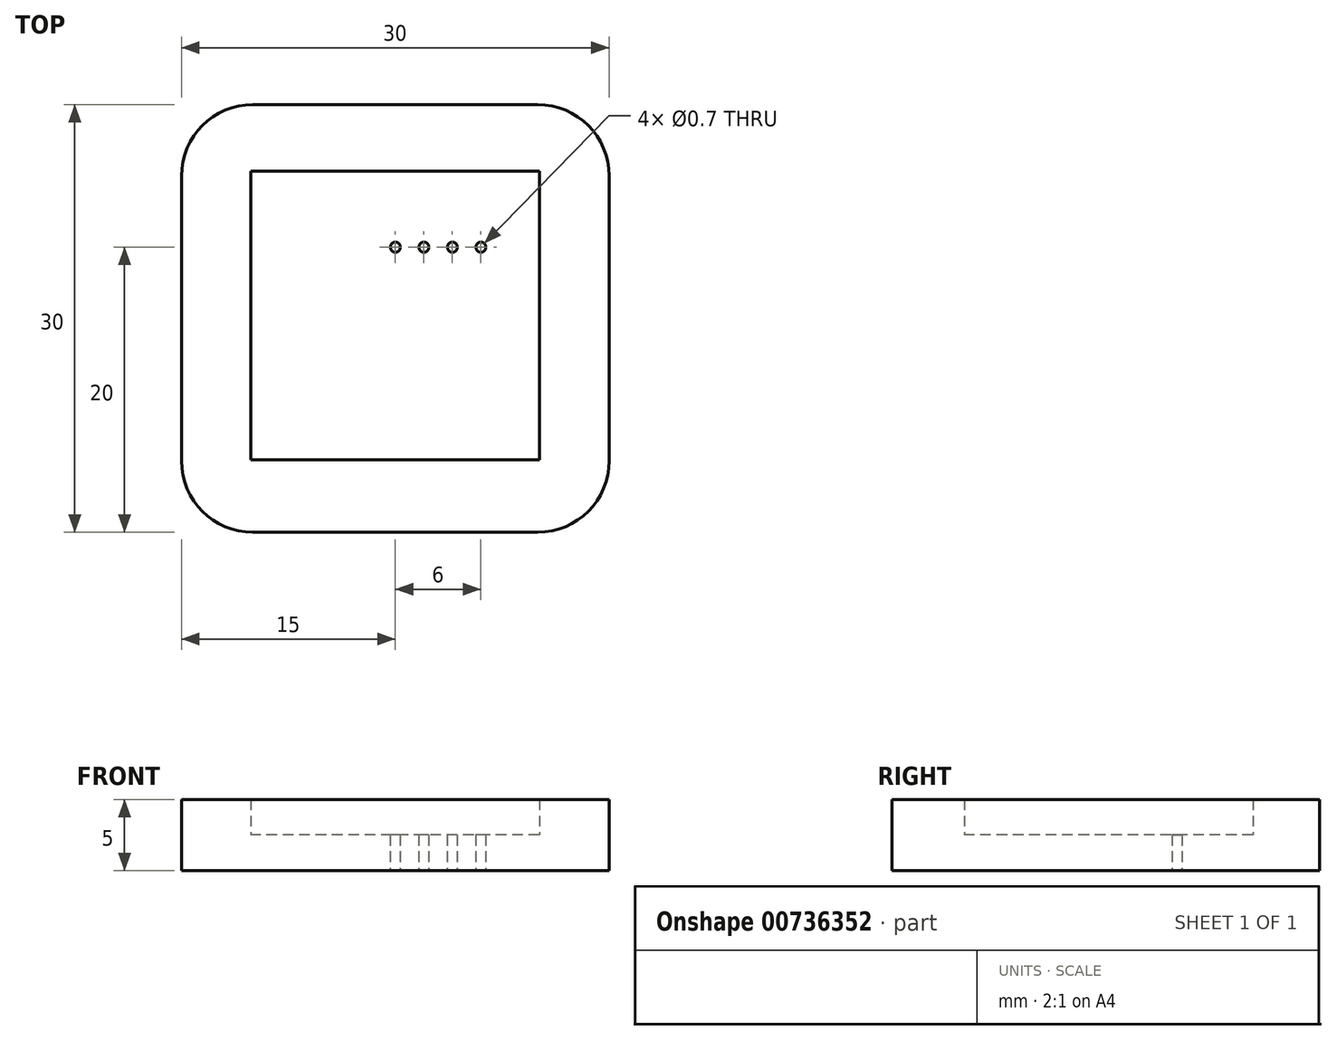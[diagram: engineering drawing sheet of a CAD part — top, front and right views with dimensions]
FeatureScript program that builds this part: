
annotation { "Feature Type Name" : "Feature", "Feature Type Description" : "" }
export const myFeature = defineFeature(function(context is Context, id is Id, definition is map)
    precondition{}
    {
        {
            var Q0;
            Q0=qCreatedBy(makeId("Top.planeOp"),FACE);
            var sketch = newSketch(context, id + "F0", { "sketchPlane" : qUnion([Q0])});
            skPoint(sketch, "E0.middle", {"position": v(0, 0) * mm});
            skCircle(sketch, "E1", {"center": v(17, 20) * mm, "radius": 0.35 * mm});
            skCircle(sketch, "E2", {"center": v(19, 20) * mm, "radius": 0.35 * mm});
            skCircle(sketch, "E3", {"center": v(15, 20) * mm, "radius": 0.35 * mm});
            skCircle(sketch, "E4", {"center": v(21, 20) * mm, "radius": 0.35 * mm});
            skLineSegment(sketch, "E5.bottom", {"start": v(0, 0) * mm, "end": v(30, 0) * mm});
            skLineSegment(sketch, "E5.top", {"start": v(0, 30) * mm, "end": v(30, 30) * mm});
            skLineSegment(sketch, "E5.left", {"start": v(0, 0) * mm, "end": v(0, 30) * mm});
            skLineSegment(sketch, "E5.right", {"start": v(30, 0) * mm, "end": v(30, 30) * mm});
            skSolve(sketch);
        }
        {
            var Q0;
            Q0 = qSketchRegion(id + "F0", true);
            extrude(context, id + "F1", {"entities" : qUnion([Q0]), "depth" : 2.5 * mm, "offsetDistance" : 25 * mm});
        }
        {
            var Q0;
            Q0=qCreatedBy(makeId("Top.planeOp"),FACE);
            var sketch = newSketch(context, id + "F2", { "sketchPlane" : qUnion([Q0])});
            skLineSegment(sketch, "E6.bottom", {"start": v(0, 0) * mm, "end": v(30, 0) * mm});
            skLineSegment(sketch, "E6.top", {"start": v(0, 30) * mm, "end": v(30, 30) * mm});
            skLineSegment(sketch, "E6.left", {"start": v(0, 0) * mm, "end": v(0, 30) * mm});
            skLineSegment(sketch, "E6.right", {"start": v(30, 0) * mm, "end": v(30, 30) * mm});
            skLineSegment(sketch, "E7.bottom", {"start": v(4.85, 5.1) * mm, "end": v(25.1, 5.1) * mm});
            skLineSegment(sketch, "E7.top", {"start": v(4.85, 25.34) * mm, "end": v(25.1, 25.34) * mm});
            skLineSegment(sketch, "E7.left", {"start": v(4.85, 5.1) * mm, "end": v(4.85, 25.34) * mm});
            skLineSegment(sketch, "E7.right", {"start": v(25.1, 5.1) * mm, "end": v(25.1, 25.34) * mm});
            skSolve(sketch);
        }
        {
            var Q0;
            Q0 = qSketchRegion(id + "F2", true);
            extrude(context, id + "F3", {"entities" : qUnion([Q0]), "operationType" : NewBodyOperationType.ADD, "depth" : 5 * mm, "offsetDistance" : 25 * mm});
        }
        {
            var Q0;
            Q0=makeQuery(id+"F3.boolean.opBoolean","MERGE",EDGE,{"derivedFrom":[makeQuery(id+"F1.opExtrude","SWEPT_EDGE",EDGE,{"disambiguationData":[OSD([sQuery(id+"F0.wireOp",EDGE,"E5.top"),sQuery(id+"F0.wireOp",EDGE,"E5.left")])]}),makeQuery(id+"F3.opExtrude","SWEPT_EDGE",EDGE,{"disambiguationData":[OSD([sQuery(id+"F2.wireOp",EDGE,"E6.top"),sQuery(id+"F2.wireOp",EDGE,"E6.left")])]})]});
            var Q1;
            Q1=makeQuery(id+"F3.boolean.opBoolean","MERGE",EDGE,{"derivedFrom":[makeQuery(id+"F1.opExtrude","SWEPT_EDGE",EDGE,{"disambiguationData":[OSD([sQuery(id+"F0.wireOp",EDGE,"E5.bottom"),sQuery(id+"F0.wireOp",EDGE,"E5.left")])]}),makeQuery(id+"F3.opExtrude","SWEPT_EDGE",EDGE,{"disambiguationData":[OSD([sQuery(id+"F2.wireOp",EDGE,"E6.bottom"),sQuery(id+"F2.wireOp",EDGE,"E6.left")])]})]});
            var Q2;
            Q2=makeQuery(id+"F3.boolean.opBoolean","MERGE",EDGE,{"derivedFrom":[makeQuery(id+"F1.opExtrude","SWEPT_EDGE",EDGE,{"disambiguationData":[OSD([sQuery(id+"F0.wireOp",EDGE,"E5.top"),sQuery(id+"F0.wireOp",EDGE,"E5.right")])]}),makeQuery(id+"F3.opExtrude","SWEPT_EDGE",EDGE,{"disambiguationData":[OSD([sQuery(id+"F2.wireOp",EDGE,"E6.top"),sQuery(id+"F2.wireOp",EDGE,"E6.right")])]})]});
            var Q3;
            Q3=makeQuery(id+"F3.boolean.opBoolean","MERGE",EDGE,{"derivedFrom":[makeQuery(id+"F1.opExtrude","SWEPT_EDGE",EDGE,{"disambiguationData":[OSD([sQuery(id+"F0.wireOp",EDGE,"E5.bottom"),sQuery(id+"F0.wireOp",EDGE,"E5.right")])]}),makeQuery(id+"F3.opExtrude","SWEPT_EDGE",EDGE,{"disambiguationData":[OSD([sQuery(id+"F2.wireOp",EDGE,"E6.bottom"),sQuery(id+"F2.wireOp",EDGE,"E6.right")])]})]});
            fillet(context, id + "F4", {"entities" : qUnion([Q0, Q1, Q2, Q3]), "radius" : 5 * mm, "tangentPropagation" : true, "allowEdgeOverflow" : false});
        }
    });
